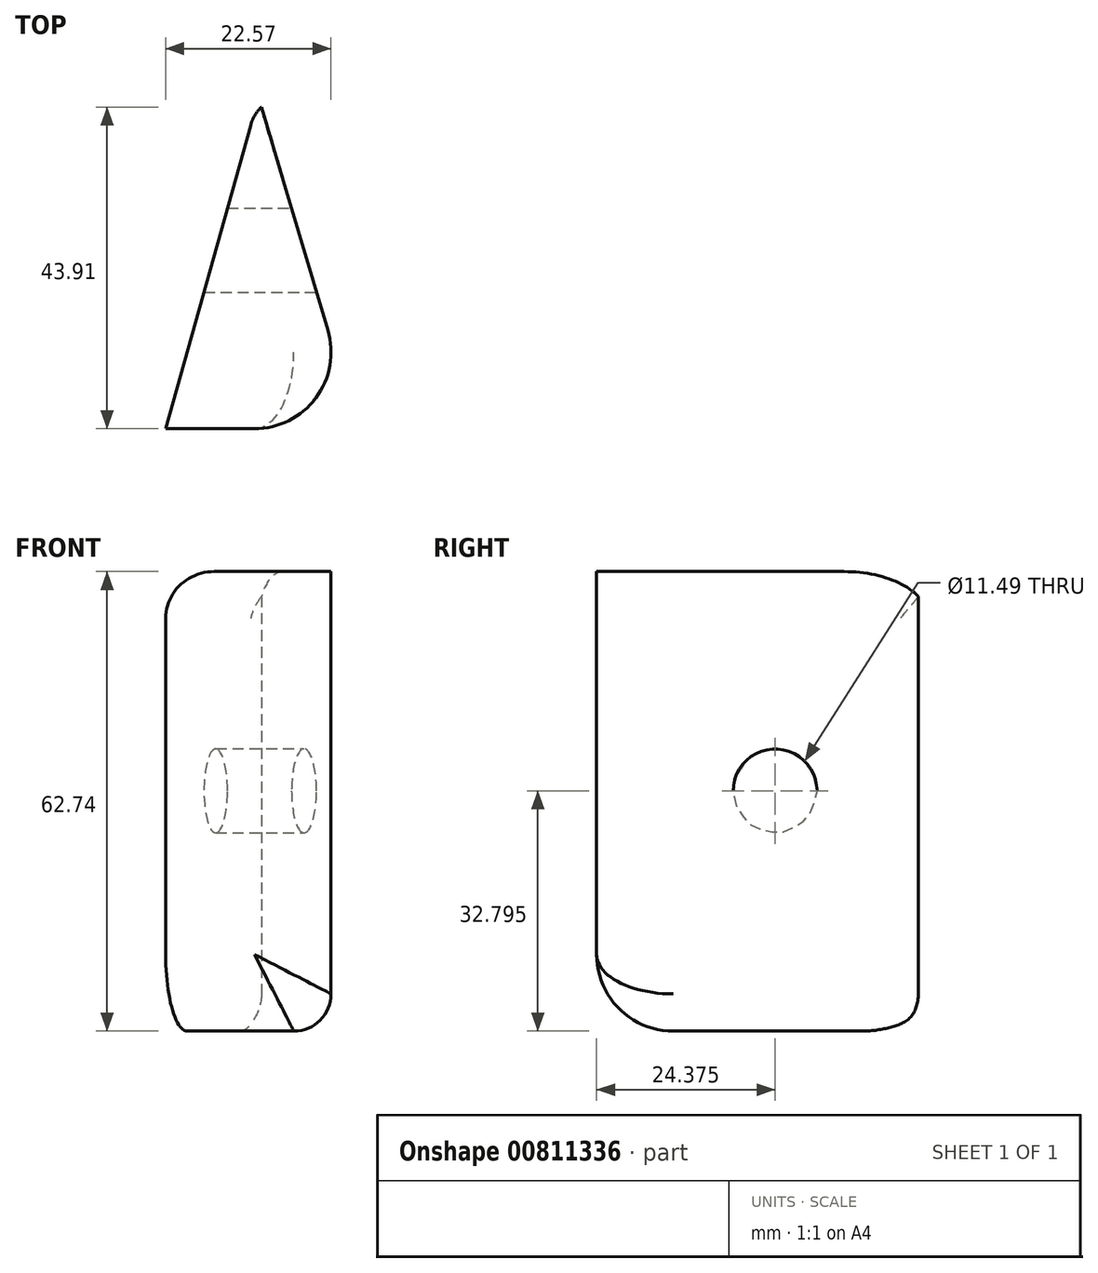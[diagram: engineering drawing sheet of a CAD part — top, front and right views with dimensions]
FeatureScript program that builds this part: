
annotation { "Feature Type Name" : "Feature", "Feature Type Description" : "" }
export const myFeature = defineFeature(function(context is Context, id is Id, definition is map)
    precondition{}
    {
        {
            var Q0;
            Q0=qCreatedBy(makeId("Top.planeOp"),FACE);
            var sketch = newSketch(context, id + "F0", { "sketchPlane" : qUnion([Q0])});
            skLineSegment(sketch, "E0", {"start": v(-40.38, -42.2) * mm, "end": v(-14.25, -42.2) * mm});
            skLineSegment(sketch, "E1", {"start": v(-14.25, -42.2) * mm, "end": v(-27.31, 1.71) * mm});
            skLineSegment(sketch, "E2", {"start": v(-27.31, 4.5) * mm, "end": v(-40.38, -42.2) * mm});
            skLineSegment(sketch, "E3", {"start": v(-27.31, 1.71) * mm, "end": v(-27.31, 4.5) * mm});
            skSolve(sketch);
        }
        {
            var Q0;
            Q0=makeQuery(id+"F0.imprint","IMPRINT",FACE,{"disambiguationData":[TD([[makeQuery(id+"F0.imprint","IMPRINT",EDGE,{"derivedFrom":sQuery(id+"F0.wireOp",EDGE,"E0")}),1.0]])]});
            extrude(context, id + "F1", {"entities" : qUnion([Q0]), "depth" : 62.74 * mm, "offsetDistance" : 25.4 * mm});
        }
        {
            var Q0;
            Q0=makeQuery(id+"F1.opExtrude","CAP_EDGE",EDGE,{"disambiguationData":[OSD([sQuery(id+"F0.wireOp",EDGE,"E2")])],"isStart":false});
            fillet(context, id + "F2", {"entities" : qUnion([Q0]), "radius" : 6.38 * mm, "tangentPropagation" : true, "allowEdgeOverflow" : false});
        }
        {
            var Q0;
            Q0=makeQuery(id+"F1.opExtrude","SWEPT_EDGE",EDGE,{"disambiguationData":[OSD([sQuery(id+"F0.wireOp",EDGE,"E2"),sQuery(id+"F0.wireOp",EDGE,"E3")])]});
            fillet(context, id + "F3", {"entities" : qUnion([Q0]), "radius" : 5.5 * mm, "tangentPropagation" : true, "allowEdgeOverflow" : false});
        }
        {
            var Q0;
            Q0=makeQuery(id+"F1.opExtrude","CAP_EDGE",EDGE,{"disambiguationData":[OSD([sQuery(id+"F0.wireOp",EDGE,"E1")])],"isStart":true});
            fillet(context, id + "F4", {"entities" : qUnion([Q0]), "radius" : 5.08 * mm, "tangentPropagation" : true, "allowEdgeOverflow" : false});
        }
        {
            var Q0;
            Q0=makeQuery(id+"F1.opExtrude","SWEPT_EDGE",EDGE,{"disambiguationData":[OSD([sQuery(id+"F0.wireOp",EDGE,"E0"),sQuery(id+"F0.wireOp",EDGE,"E1")])]});
            fillet(context, id + "F5", {"entities" : qUnion([Q0]), "radius" : 10.46 * mm, "tangentPropagation" : true, "allowEdgeOverflow" : false});
        }
        {
            var Q0;
            Q0=qCreatedBy(makeId("Right.planeOp"),FACE);
            var sketch = newSketch(context, id + "F6", { "sketchPlane" : qUnion([Q0])});
            skCircle(sketch, "E4", {"center": v(-17.83, 32.8) * mm, "radius": 5.75 * mm});
            skSolve(sketch);
        }
        {
            var Q0;
            Q0 = qSketchRegion(id + "F6", true);
            extrude(context, id + "F7", {"entities" : qUnion([Q0]), "operationType" : NewBodyOperationType.REMOVE, "oppositeDirection" : true, "depth" : 46.74 * mm, "offsetDistance" : 25.4 * mm});
        }
    });
